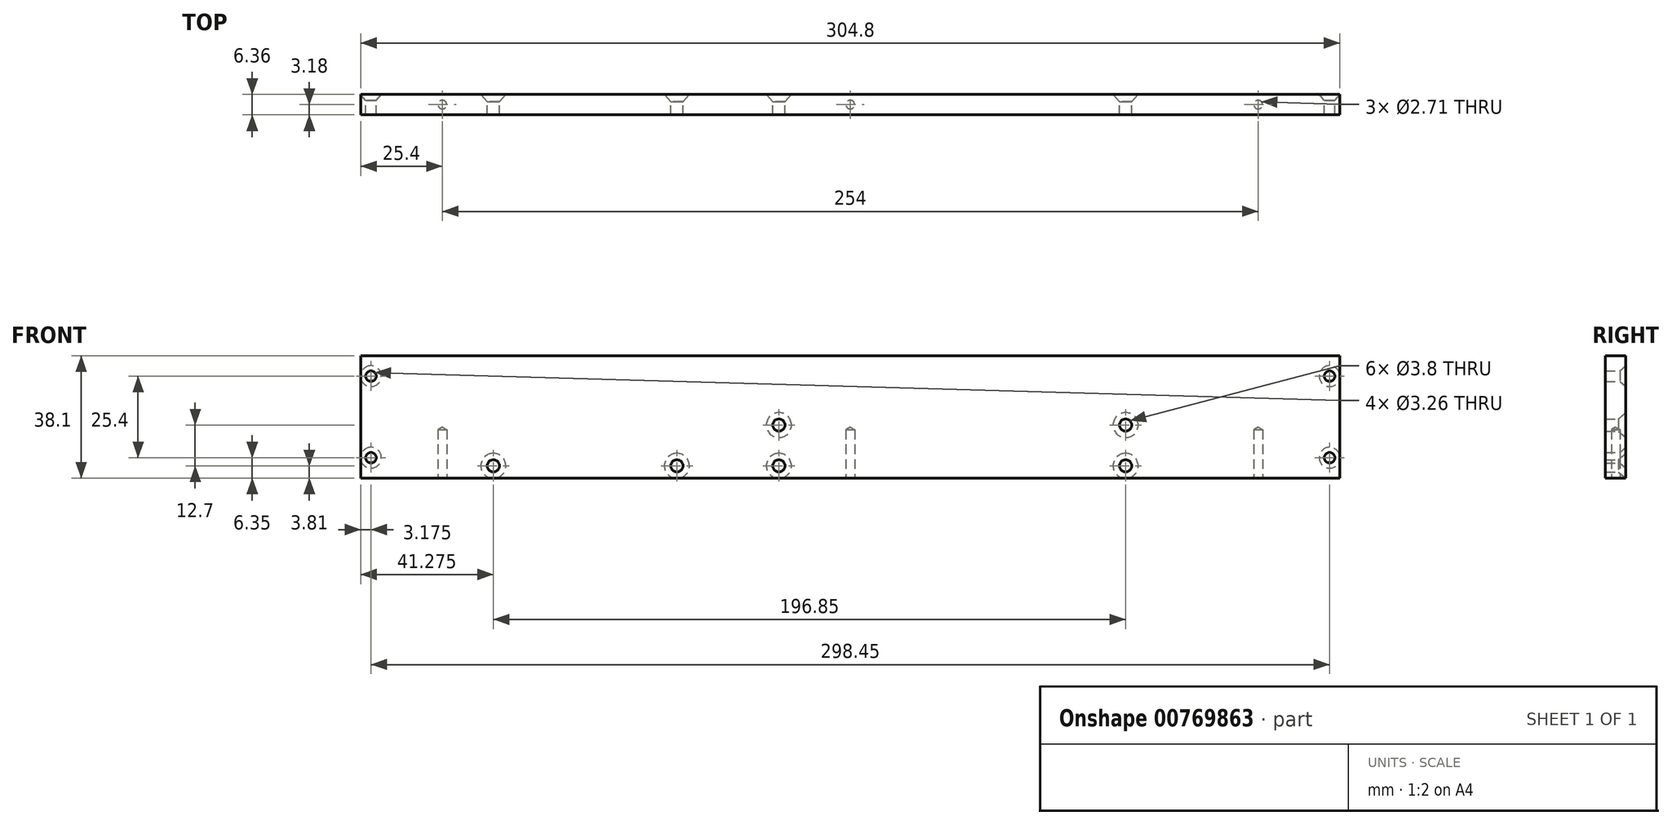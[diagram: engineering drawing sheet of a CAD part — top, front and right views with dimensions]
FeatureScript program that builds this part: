
annotation { "Feature Type Name" : "Feature", "Feature Type Description" : "" }
export const myFeature = defineFeature(function(context is Context, id is Id, definition is map)
    precondition{}
    {
        {
            var Q0;
            Q0=qCreatedBy(makeId("Top.planeOp"),FACE);
            var sketch = newSketch(context, id + "F0", { "sketchPlane" : qUnion([Q0])});
            skLineSegment(sketch, "E0.bottom", {"start": v(-152.4, 3.17) * mm, "end": v(152.4, 3.17) * mm});
            skLineSegment(sketch, "E0.top", {"start": v(-152.4, -3.18) * mm, "end": v(152.4, -3.18) * mm});
            skLineSegment(sketch, "E0.left", {"start": v(-152.4, 3.17) * mm, "end": v(-152.4, -3.18) * mm});
            skLineSegment(sketch, "E0.right", {"start": v(152.4, 3.17) * mm, "end": v(152.4, -3.18) * mm});
            skLineSegment(sketch, "E1", {"start": v(-152.4, 3.17) * mm, "end": v(152.4, -3.17) * mm, "construction": true});
            skSolve(sketch);
        }
        {
            var Q0;
            Q0=qSketchRegion(id+"F0",true);
            extrude(context, id + "F1", {"entities" : qUnion([Q0]), "depth" : 38.1 * mm, "offsetDistance" : 25.4 * mm});
        }
        {
            var Q0;
            Q0=makeQuery(id+"F1.opExtrude","CAP_FACE",FACE,{"disambiguationData":[OSD([sQuery(id+"F0.wireOp",EDGE,"E0.bottom"),sQuery(id+"F0.wireOp",EDGE,"E0.top"),sQuery(id+"F0.wireOp",EDGE,"E0.left"),sQuery(id+"F0.wireOp",EDGE,"E0.right")])],"isStart":true});
            var sketch = newSketch(context, id + "F2", { "sketchPlane" : qUnion([Q0])});
            skLineSegment(sketch, "E2", {"start": v(-152.4, 0) * mm, "end": v(152.4, 0) * mm, "construction": true});
            skPoint(sketch, "E3", {"position": v(-127, 0) * mm});
            skPoint(sketch, "E4", {"position": v(0, 0) * mm});
            skPoint(sketch, "E5", {"position": v(127, 0) * mm});
            skSolve(sketch);
        }
        {
            var Q0;
            Q0=sQuery(id+"F2.wireOp",VERTEX,"E3");
            var Q1;
            Q1=sQuery(id+"F2.wireOp",VERTEX,"E5");
            var Q2;
            Q2=sQuery(id+"F2.wireOp",VERTEX,"E4");
            var Q3;
            Q3=makeQuery(id+"F1.opExtrude","SWEPT_BODY",BODY,{"disambiguationData":[OSD([sQuery(id+"F0.wireOp",EDGE,"E0.bottom"),sQuery(id+"F0.wireOp",EDGE,"E0.top"),sQuery(id+"F0.wireOp",EDGE,"E0.left"),sQuery(id+"F0.wireOp",EDGE,"E0.right")])]});
            hole(context, id + "F3", {"style" : HoleStyle.SIMPLE, "endStyle" : HoleEndStyle.BLIND, "standardTappedOrClearance" : lookupTablePath({ "standard" : "ANSI", "engagement" : "75%", "pitch" : "32 tpi", "size" : "#6", "type" : "Tapped" }), "standardBlindInLast" : lookupTablePath({ "standard" : "ANSI", "engagement" : "75%", "pitch" : "32 tpi", "size" : "#6", "type" : "Tapped" }), "holeDiameter" : 2.7 * mm, "majorDiameter" : 3.5 * mm, "showTappedDepth" : true, "holeDepth" : 15.08 * mm, "tappedDepth" : 12.7 * mm, "tapClearance" : 3, "locations" : qUnion([Q0, Q1, Q2]), "scope" : qUnion([Q3])});
        }
        {
            var Q0;
            Q0=makeQuery(id+"F1.opExtrude","SWEPT_FACE",FACE,{"disambiguationData":[OSD([sQuery(id+"F0.wireOp",EDGE,"E0.bottom")])]});
            var sketch = newSketch(context, id + "F4", { "sketchPlane" : qUnion([Q0])});
            skLineSegment(sketch, "E6", {"start": v(149.22, 38.1) * mm, "end": v(149.22, 0) * mm, "construction": true});
            skLineSegment(sketch, "E7", {"start": v(-149.22, 38.1) * mm, "end": v(-149.22, 0) * mm, "construction": true});
            skPoint(sketch, "E8", {"position": v(149.22, 31.75) * mm});
            skPoint(sketch, "E9", {"position": v(149.22, 6.35) * mm});
            skPoint(sketch, "E10", {"position": v(-149.22, 31.75) * mm});
            skPoint(sketch, "E11", {"position": v(-149.22, 6.35) * mm});
            skPoint(sketch, "E12", {"position": v(149.22, 19.05) * mm});
            skPoint(sketch, "E13", {"position": v(-149.22, 19.05) * mm});
            skSolve(sketch);
        }
        {
            var Q0;
            Q0=sQuery(id+"F4.wireOp",VERTEX,"E8");
            var Q1;
            Q1=sQuery(id+"F4.wireOp",VERTEX,"E9");
            var Q2;
            Q2=sQuery(id+"F4.wireOp",VERTEX,"E10");
            var Q3;
            Q3=sQuery(id+"F4.wireOp",VERTEX,"E11");
            var Q4;
            Q4=makeQuery(id+"F1.opExtrude","SWEPT_BODY",BODY,{"disambiguationData":[OSD([sQuery(id+"F0.wireOp",EDGE,"E0.bottom"),sQuery(id+"F0.wireOp",EDGE,"E0.top"),sQuery(id+"F0.wireOp",EDGE,"E0.left"),sQuery(id+"F0.wireOp",EDGE,"E0.right")])]});
            hole(context, id + "F5", {"style" : HoleStyle.C_SINK, "endStyle" : HoleEndStyle.THROUGH, "standardTappedOrClearance" : lookupTablePath({ "standard" : "ANSI", "fit" : "Normal (ASME)", "size" : "#4", "type" : "Clearance" }), "standardBlindInLast" : lookupTablePath({ "fit" : "Free", "standard" : "ANSI", "size" : "#4", "type" : "Clearance" }), "holeDiameter" : 3.26 * mm, "cSinkDiameter" : 6.48 * mm, "cSinkAngle" : 82 * degree, "majorDiameter" : 2.84 * mm, "tappedDepth" : 11.84 * mm, "tapClearance" : 3, "startFromSketch" : true, "locations" : qUnion([Q0, Q1, Q2, Q3]), "scope" : qUnion([Q4])});
        }
        {
            var Q0;
            Q0=makeQuery(id+"F1.opExtrude","SWEPT_FACE",FACE,{"disambiguationData":[OSD([sQuery(id+"F0.wireOp",EDGE,"E0.bottom")])]});
            var sketch = newSketch(context, id + "F6", { "sketchPlane" : qUnion([Q0])});
            skLineSegment(sketch, "E14", {"start": v(-152.4, 3.81) * mm, "end": v(152.4, 3.81) * mm, "construction": true});
            skPoint(sketch, "E15", {"position": v(-85.72, 3.81) * mm});
            skPoint(sketch, "E16", {"position": v(22.23, 3.81) * mm});
            skPoint(sketch, "E17", {"position": v(53.98, 3.81) * mm});
            skPoint(sketch, "E18", {"position": v(111.12, 3.81) * mm});
            skPoint(sketch, "E19", {"position": v(-85.72, 16.51) * mm});
            skPoint(sketch, "E20", {"position": v(22.23, 16.51) * mm});
            skSolve(sketch);
        }
        {
            var Q0;
            Q0=sQuery(id+"F6.wireOp",VERTEX,"E15");
            var Q1;
            Q1=sQuery(id+"F6.wireOp",VERTEX,"E16");
            var Q2;
            Q2=sQuery(id+"F6.wireOp",VERTEX,"E17");
            var Q3;
            Q3=sQuery(id+"F6.wireOp",VERTEX,"E18");
            var Q4;
            Q4=sQuery(id+"F6.wireOp",VERTEX,"E19");
            var Q5;
            Q5=sQuery(id+"F6.wireOp",VERTEX,"E20");
            var Q6;
            Q6=makeQuery(id+"F1.opExtrude","SWEPT_BODY",BODY,{"disambiguationData":[OSD([sQuery(id+"F0.wireOp",EDGE,"E0.bottom"),sQuery(id+"F0.wireOp",EDGE,"E0.top"),sQuery(id+"F0.wireOp",EDGE,"E0.left"),sQuery(id+"F0.wireOp",EDGE,"E0.right")])]});
            hole(context, id + "F7", {"style" : HoleStyle.C_SINK, "endStyle" : HoleEndStyle.THROUGH, "standardTappedOrClearance" : lookupTablePath({ "fit" : "Free", "standard" : "ANSI", "size" : "#6", "type" : "Clearance" }), "standardBlindInLast" : lookupTablePath({ "fit" : "Free", "standard" : "ANSI", "engagement" : "75%", "pitch" : "32 tpi", "size" : "#6", "type" : "Clearance & tapped" }), "holeDiameter" : 3.8 * mm, "cSinkDiameter" : 7.8 * mm, "cSinkAngle" : 82 * degree, "majorDiameter" : 3.5 * mm, "tappedDepth" : 6.5 * mm, "tapClearance" : 3, "locations" : qUnion([Q0, Q1, Q2, Q3, Q4, Q5]), "scope" : qUnion([Q6])});
        }
    });
